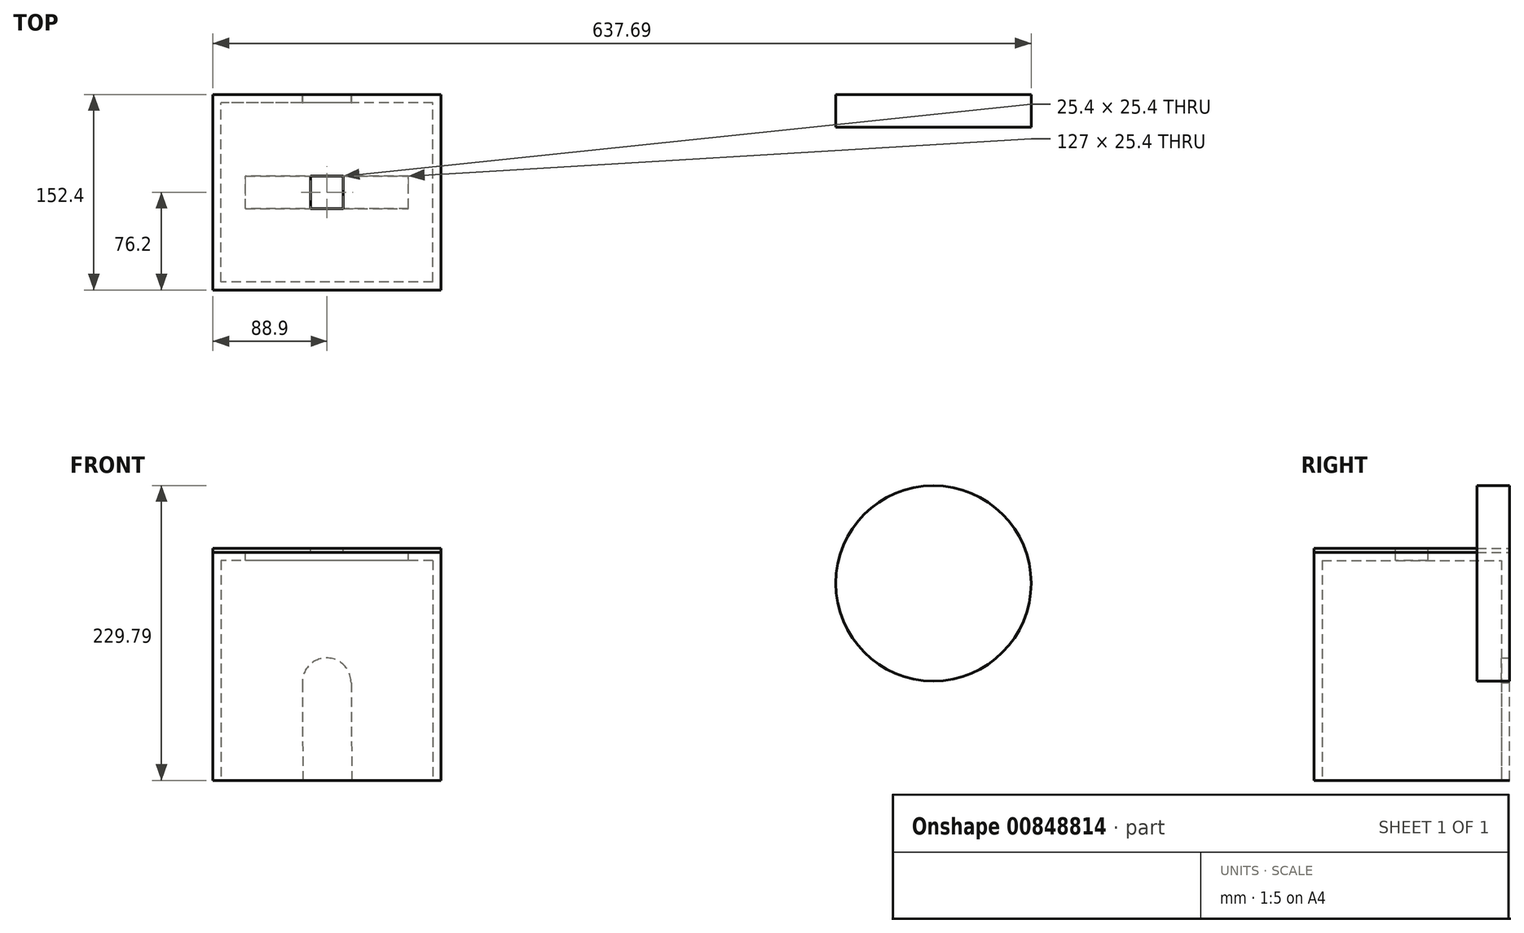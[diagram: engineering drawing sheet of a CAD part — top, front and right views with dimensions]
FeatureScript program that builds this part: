
annotation { "Feature Type Name" : "Feature", "Feature Type Description" : "" }
export const myFeature = defineFeature(function(context is Context, id is Id, definition is map)
    precondition{}
    {
        {
            var Q0;
            Q0=qCreatedBy(makeId("Front.planeOp"),FACE);
            var sketch = newSketch(context, id + "F0", { "sketchPlane" : qUnion([Q0])});
            skLineSegment(sketch, "E0.bottom", {"start": v(0, 0) * mm, "end": v(-177.8, 0) * mm});
            skLineSegment(sketch, "E0.top", {"start": v(0, -177.8) * mm, "end": v(-177.8, -177.8) * mm});
            skLineSegment(sketch, "E0.left", {"start": v(0, 0) * mm, "end": v(0, -177.8) * mm});
            skLineSegment(sketch, "E0.right", {"start": v(-177.8, 0) * mm, "end": v(-177.8, -177.8) * mm});
            skSolve(sketch);
        }
        {
            var Q0;
            Q0 = qSketchRegion(id + "F0", true);
            extrude(context, id + "F1", {"entities" : qUnion([Q0]), "depth" : 152.4 * mm, "offsetDistance" : 25.4 * mm});
        }
        {
            var Q0;
            Q0=makeQuery(id+"F1.opExtrude","SWEPT_FACE",FACE,{"disambiguationData":[OSD([sQuery(id+"F0.wireOp",EDGE,"E0.top")])]});
            shell(context, id + "F2", {"entities" : qUnion([Q0]), "thickness" : 6.35 * mm});
        }
        {
            var Q0;
            Q0=makeQuery(id+"F1.opExtrude","CAP_FACE",FACE,{"disambiguationData":[OSD([sQuery(id+"F0.wireOp",EDGE,"E0.bottom"),sQuery(id+"F0.wireOp",EDGE,"E0.top"),sQuery(id+"F0.wireOp",EDGE,"E0.left"),sQuery(id+"F0.wireOp",EDGE,"E0.right")])],"isStart":true});
            var sketch = newSketch(context, id + "F3", { "sketchPlane" : qUnion([Q0])});
            skLineSegment(sketch, "E1.bottom", {"start": v(69.62, -177.8) * mm, "end": v(107.72, -177.8) * mm});
            skLineSegment(sketch, "E1.left", {"start": v(69.62, -177.8) * mm, "end": v(70.08, -101.6) * mm});
            skLineSegment(sketch, "E1.right", {"start": v(107.72, -177.8) * mm, "end": v(108.18, -101.6) * mm});
            skArc(sketch, "E2", {"start": v(108.18, -101.6) * mm, "mid": v(89.13, -82.44) * mm, "end": v(70.08, -101.6) * mm});
            skLineSegment(sketch, "E3", {"start": v(69.85, -139.7) * mm, "end": v(0, -139.7) * mm, "construction": true});
            skLineSegment(sketch, "E4", {"start": v(107.95, -139.7) * mm, "end": v(177.8, -139.7) * mm, "construction": true});
            skSolve(sketch);
        }
        {
            var Q0;
            Q0 = qSketchRegion(id + "F3", true);
            extrude(context, id + "F4", {"entities" : qUnion([Q0]), "operationType" : NewBodyOperationType.REMOVE, "oppositeDirection" : true, "depth" : 25.4 * mm, "offsetDistance" : 25.4 * mm});
        }
        {
            var Q0;
            Q0=qCreatedBy(makeId("Front.planeOp"),FACE);
            var sketch = newSketch(context, id + "F5", { "sketchPlane" : qUnion([Q0])});
            skCircle(sketch, "E5", {"center": v(383.7, -24.2) * mm, "radius": 76.2 * mm});
            skSolve(sketch);
        }
        {
            var Q0;
            Q0 = qSketchRegion(id + "F5", true);
            extrude(context, id + "F6", {"entities" : qUnion([Q0]), "depth" : 25.4 * mm, "offsetDistance" : 25.4 * mm});
        }
        {
            var Q0;
            Q0=makeQuery(id+"F1.opExtrude","SWEPT_FACE",FACE,{"disambiguationData":[OSD([sQuery(id+"F0.wireOp",EDGE,"E0.bottom")])]});
            var sketch = newSketch(context, id + "F7", { "sketchPlane" : qUnion([Q0])});
            skLineSegment(sketch, "E6.bottom", {"start": v(-152.4, -88.9) * mm, "end": v(-25.4, -88.9) * mm});
            skLineSegment(sketch, "E6.top", {"start": v(-152.4, -63.5) * mm, "end": v(-25.4, -63.5) * mm});
            skLineSegment(sketch, "E6.left", {"start": v(-152.4, -88.9) * mm, "end": v(-152.4, -63.5) * mm});
            skLineSegment(sketch, "E6.right", {"start": v(-25.4, -88.9) * mm, "end": v(-25.4, -63.5) * mm});
            skLineSegment(sketch, "E7", {"start": v(-88.9, -88.9) * mm, "end": v(-88.9, -152.4) * mm, "construction": true});
            skPoint(sketch, "E7.endSnap0", {"position": v(-88.9, -152.4) * mm});
            skLineSegment(sketch, "E8", {"start": v(-88.9, -63.5) * mm, "end": v(-88.9, 0) * mm, "construction": true});
            skLineSegment(sketch, "E9", {"start": v(-177.8, -76.2) * mm, "end": v(-152.4, -76.2) * mm, "construction": true});
            skLineSegment(sketch, "E10", {"start": v(-25.4, -76.2) * mm, "end": v(0, -76.2) * mm, "construction": true});
            skSolve(sketch);
        }
        {
            var Q0;
            Q0 = qSketchRegion(id + "F7", true);
            extrude(context, id + "F8", {"entities" : qUnion([Q0]), "operationType" : NewBodyOperationType.REMOVE, "oppositeDirection" : true, "depth" : 25.4 * mm, "offsetDistance" : 25.4 * mm});
        }
        {
            var Q0;
            Q0=makeQuery(id+"F1.opExtrude","SWEPT_FACE",FACE,{"disambiguationData":[OSD([sQuery(id+"F0.wireOp",EDGE,"E0.bottom")])]});
            var sketch = newSketch(context, id + "F9", { "sketchPlane" : qUnion([Q0])});
            skLineSegment(sketch, "E11.0", {"start": v(-177.8, -152.4) * mm, "end": v(-177.8, 0) * mm});
            skLineSegment(sketch, "E12.0", {"start": v(0, -152.4) * mm, "end": v(-177.8, -152.4) * mm});
            skLineSegment(sketch, "E13.0", {"start": v(0, -152.4) * mm, "end": v(0, 0) * mm});
            skLineSegment(sketch, "E14.0", {"start": v(0, 0) * mm, "end": v(-177.8, 0) * mm});
            skSolve(sketch);
        }
        {
            var Q0;
            Q0 = qSketchRegion(id + "F9", true);
            extrude(context, id + "F10", {"entities" : qUnion([Q0]), "depth" : 3.17 * mm, "offsetDistance" : 25.4 * mm});
        }
        {
            var Q0;
            Q0=makeQuery(id+"F10.opExtrude","CAP_FACE",FACE,{"disambiguationData":[OSD([sQuery(id+"F9.wireOp",EDGE,"E11.0"),sQuery(id+"F9.wireOp",EDGE,"E12.0"),sQuery(id+"F9.wireOp",EDGE,"E13.0"),sQuery(id+"F9.wireOp",EDGE,"E14.0")])],"isStart":false});
            var sketch = newSketch(context, id + "F11", { "sketchPlane" : qUnion([Q0])});
            skLineSegment(sketch, "E15.bottom", {"start": v(-101.6, -88.9) * mm, "end": v(-76.2, -88.9) * mm});
            skLineSegment(sketch, "E15.top", {"start": v(-101.6, -63.5) * mm, "end": v(-76.2, -63.5) * mm});
            skLineSegment(sketch, "E15.left", {"start": v(-101.6, -88.9) * mm, "end": v(-101.6, -63.5) * mm});
            skLineSegment(sketch, "E15.right", {"start": v(-76.2, -88.9) * mm, "end": v(-76.2, -63.5) * mm});
            skLineSegment(sketch, "E16", {"start": v(-177.8, -76.2) * mm, "end": v(0, -76.2) * mm, "construction": true});
            skLineSegment(sketch, "E17", {"start": v(-88.9, -152.4) * mm, "end": v(-88.9, 0) * mm, "construction": true});
            skSolve(sketch);
        }
        {
            var Q0;
            Q0 = qSketchRegion(id + "F11", true);
            extrude(context, id + "F12", {"entities" : qUnion([Q0]), "operationType" : NewBodyOperationType.REMOVE, "oppositeDirection" : true, "depth" : 25.4 * mm, "offsetDistance" : 25.4 * mm});
        }
    });
